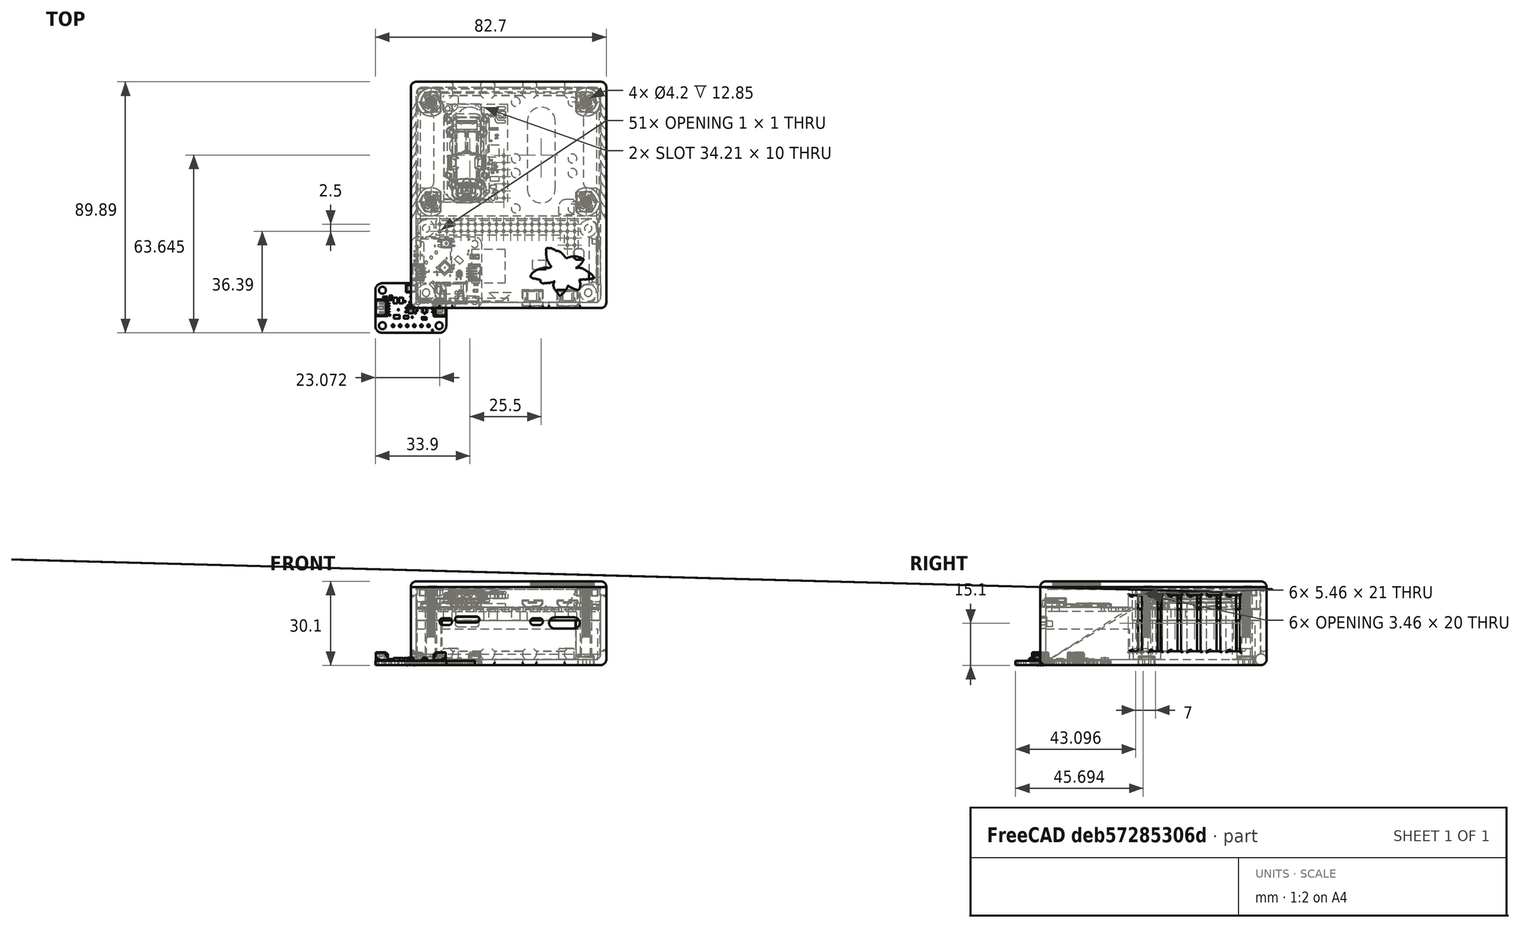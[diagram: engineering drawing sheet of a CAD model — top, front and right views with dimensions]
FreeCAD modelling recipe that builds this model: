
FCSTD DOCUMENT  (FreeCAD 0.20R29410 (Git))
Label: wearableV5
License: All rights reserved
LicenseURL: http://en.wikipedia.org/wiki/All_rights_reserved
objects: Part::Feature×60, Part::Cylinder×20, Part::MultiFuse×16, Part::Fillet×13, Sketcher::SketchObject×13, Part::Extrusion×13, App::Part×9, Part::Box×6, Part::Cut×6, Mesh::Feature×2, Part::Compound×1
note: 148 computed .brp shape members not serialized (recipe doc carries the construction recipe); baked Part::Feature solids carry a one-line shape summary decoded from their .brp

FEATURE [Part::Box] Box  label="battery"
  AttacherType = Attacher::AttachEngine3D
  Height = 11
  Length = 65
  Placement = pos=(2,2,2) rot=(0,0,1;0rad)
  Width = 30
FEATURE [Mesh::Feature] pisugar3Board
  Placement = pos=(-4.89,35.08,0.25) rot=(-1,0,0;4.71239rad)
FEATURE [Part::Feature] Part__Feature001  label="RaspberryPiZeroW"
  Placement = pos=(34.5,17,19.18) rot=(1,0,0;1.5708rad)
  shape: bbox 65.9 x 31.25 x 4.8 mm, 368 faces, 2 solids (baked)
FEATURE [Part::Feature] Part__Feature  label="ips7100"
  Placement = pos=(-24,0,222) rot=(0.999993,-0.003655,0;3.14159rad)
  shape: bbox 48.14 x 14.05 x 44.14 mm, 1935 faces (baked)
FEATURE [Part::Compound] Compound  label="ips7100s"
  Links = -> [Part__Feature]
  Placement = pos=(11.15,32.5,15.79) rot=(0,0.707107,0.707107;3.15032rad)
FEATURE [Part::Feature] Part__Feature002  label="Printed Circuit Board"
  shape: bbox 25.4 x 17.78 x 1.6 mm, 42 faces (baked)
FEATURE [Part::Feature] Part__Feature003  label="EAHC2835WD6"
  shape: bbox 3.513 x 2.813 x 0.7485 mm, 108 faces, 4 solids (baked)
FEATURE [Part::Feature] Part__Feature004  label="AS7341 v2"
  Placement = pos=(0,-0.339822,1.6) rot=(0,0,1;0rad)
  shape: bbox 2 x 3.1 x 1.1 mm, 267 faces, 26 solids (baked)
FEATURE [Part::Feature] Part__Feature005  label="CAPC-0805-T0.95-BN v1"
  Placement = pos=(-5.01759,-3.15294,1.6) rot=(0,0,1;0rad)
  shape: bbox 2.1 x 1.35 x 0.95 mm, 42 faces (baked)
FEATURE [Part::Feature] Part__Feature006  label="CAPC-0805-T0.95-BN v002"
  Placement = pos=(-5.48627,2.66154,1.6) rot=(0,0,-1;1.5708rad)
  shape: bbox 1.35 x 2.1 x 0.95 mm, 42 faces (baked)
FEATURE [Part::Feature] Part__Feature007  label="CAPC-0805-T0.95-BN v003"
  Placement = pos=(-3.43627,2.66154,1.6) rot=(0,0,-1;1.5708rad)
  shape: bbox 1.35 x 2.1 x 0.95 mm, 42 faces (baked)
FEATURE [Part::Feature] Part__Feature008  label="CAPC-0603-T0.9-BN v1"
  Placement = pos=(-1.69987,-3.28475,1.6) rot=(0,0,1;0rad)
  shape: bbox 1.7 x 0.9 x 0.9 mm, 42 faces (baked)
FEATURE [Part::Feature] Part__Feature009  label="BODY_MF06A"
  Placement = pos=(0,0,0.762) rot=(0.57735,-0.57735,-0.57735;2.0944rad)
  shape: bbox 1.601 x 2.921 x 1.016 mm, 42 faces (baked)
FEATURE [Part::Feature] Part__Feature010  label="LEAD_MF06A"
  Placement = pos=(-0.9652,-0.9525,0.1016) rot=(0.57735,-0.57735,-0.57735;2.0944rad)
  shape: bbox 0.6223 x 0.3749 x 0.8636 mm, 14 faces (baked)
FEATURE [Part::Feature] Part__Feature011  label="LEAD_MF06A001"
  Placement = pos=(-0.9652,0,0.1016) rot=(0.57735,-0.57735,-0.57735;2.0944rad)
  shape: bbox 0.6223 x 0.3749 x 0.8636 mm, 14 faces (baked)
FEATURE [Part::Feature] Part__Feature012  label="LEAD_MF06A002"
  Placement = pos=(-0.9652,0.9525,0.1016) rot=(0.57735,-0.57735,-0.57735;2.0944rad)
  shape: bbox 0.6223 x 0.3749 x 0.8636 mm, 14 faces (baked)
FEATURE [Part::Feature] Part__Feature013  label="LEAD_MF06A003"
  Placement = pos=(0.9652,-0.9525,0.1016) rot=(0.57735,0.57735,0.57735;2.0944rad)
  shape: bbox 0.6223 x 0.3749 x 0.8636 mm, 14 faces (baked)
FEATURE [Part::Feature] Part__Feature014  label="LEAD_MF06A004"
  Placement = pos=(0.9652,0,0.1016) rot=(0.57735,0.57735,0.57735;2.0944rad)
  shape: bbox 0.6223 x 0.3749 x 0.8636 mm, 14 faces (baked)
FEATURE [Part::Feature] Part__Feature015  label="LEAD_MF06A005"
  Placement = pos=(0.9652,0.9525,0.1016) rot=(0.57735,0.57735,0.57735;2.0944rad)
  shape: bbox 0.6223 x 0.3749 x 0.8636 mm, 14 faces (baked)
FEATURE [Part::Feature] Part__Feature016  label="SOT363 v2"
  Placement = pos=(4.97054,-0.645171,1.675) rot=(0,0,1;3.14159rad)
  shape: bbox 2.1 x 2 x 1.1 mm, 94 faces, 7 solids (baked)
FEATURE [Part::Feature] Part__Feature017  label="LED 0603 single color v1"
  Placement = pos=(-9.18406,3.72778,1.60762) rot=(0,0,1;1.5708rad)
  shape: bbox 1.961 x 0.7932 x 0.7145 mm, 63 faces, 5 solids (baked)
FEATURE [Part::Feature] Part__Feature018  label="RESC-0603 v1"
  Placement = pos=(4.83432,-3.67461,1.6) rot=(0,0,1;0rad)
  shape: bbox 1.7 x 0.9 x 0.55 mm, 52 faces, 3 solids (baked)
FEATURE [Part::Feature] Part__Feature019  label="RESC-0603 v002"
  Placement = pos=(-7.14949,3.61248,1.6) rot=(0,0,-1;1.5708rad)
  shape: bbox 0.9 x 1.7 x 0.55 mm, 52 faces, 3 solids (baked)
FEATURE [Part::Feature] Part__Feature020  label="YC164_RESPACK v1"
  Placement = pos=(2.99591,1.52916,1.6) rot=(0,0,1;0rad)
  shape: bbox 3.2 x 1.6 x 0.61 mm, 172 faces (baked)
FEATURE [Part::Feature] Part__Feature021  label="qwicc v2"
  Placement = pos=(-10.8364,0.0607456,1.65) rot=(0,0,-1;1.5708rad)
  shape: bbox 4.95 x 6 x 2.96 mm, 229 faces, 7 solids (baked)
FEATURE [Part::Feature] Part__Feature022  label="qwicc v003"
  Placement = pos=(10.8256,0.00556102,1.65) rot=(0,0,1;1.5708rad)
  shape: bbox 4.95 x 6 x 2.96 mm, 229 faces, 7 solids (baked)
FEATURE [Part::Feature] Part__Feature023  label="scd30"
  Placement = pos=(20,54,27) rot=(0.57735,0.57735,-0.57735;4.18879rad)
  shape: bbox 23.02 x 35.11 x 7.027 mm, 2292 faces, 25 solids (baked)
FEATURE [App::Part] sot_23_6_v2  label="sot-23-6 v2"
  Group = -> [Part__Feature009,Part__Feature010,Part__Feature011,Part__Feature012,Part__Feature013,Part__Feature014,Part__Feature015]
  Origin = -> Origin
  Placement = pos=(-4.47945,-0.603742,1.69152) rot=(0,0,1;0rad)
FEATURE [App::Part] Adafruit_AS7341_STEMMA_QT_v2  label="bme280"
  Group = -> [Part__Feature002,Part__Feature003,Part__Feature004,Part__Feature005,Part__Feature006,Part__Feature007,Part__Feature008,sot_23_6_v2,Part__Feature016,Part__Feature017,Part__Feature018,Part__Feature019,Part__Feature020,Part__Feature021,Part__Feature022]
  Origin = -> Origin001
  Placement = pos=(47.7,42,20) rot=(0,0,1;0rad)
FEATURE [Part::Box] Box002  label="bottom"
  AttacherType = Attacher::AttachEngine3D
  Height = 28
  Length = 70
  Width = 81
FEATURE [Part::Fillet] Fillet  label="bottom002"
  Base = -> Box002
  Edges = 8 edges r=2: [Edge1,Edge3,Edge4,Edge5,Edge7,Edge8,Edge9,Edge11]
FEATURE [Part::Box] Box003  label="bottom001"
  AttacherType = Attacher::AttachEngine3D
  Height = 39
  Length = 66
  Placement = pos=(2,2,2) rot=(0,0,1;0rad)
  Width = 77
FEATURE [Part::Fillet] Fillet001  label="bottomCut"
  Base = -> Box003
  Edges = 8 edges r=2: [Edge1,Edge3,Edge4,Edge5,Edge7,Edge8,Edge9,Edge11]
FEATURE [Part::Cut] Cut  label="bottom003"
  Base = -> Fillet
  Tool = -> Fillet001
FEATURE [Part::Cylinder] Cylinder
  Angle = 360
  AttacherType = Attacher::AttachEngine3D
  FirstAngle = 0
  Height = 14
  Placement = pos=(7.25,73.75,2) rot=(0,0,1;0rad)
  Radius = 5
  SecondAngle = 0
FEATURE [Part::Cylinder] Cylinder001
  Angle = 360
  AttacherType = Attacher::AttachEngine3D
  FirstAngle = 0
  Height = 14
  Placement = pos=(62.75,38,2) rot=(0,0,1;0rad)
  Radius = 5
  SecondAngle = 0
FEATURE [Part::Cylinder] Cylinder002
  Angle = 360
  AttacherType = Attacher::AttachEngine3D
  FirstAngle = 0
  Height = 14
  Placement = pos=(7.25,38,2) rot=(0,0,1;0rad)
  Radius = 5
  SecondAngle = 0
FEATURE [Part::Cylinder] Cylinder003
  Angle = 360
  AttacherType = Attacher::AttachEngine3D
  FirstAngle = 0
  Height = 14
  Placement = pos=(62.75,73.75,2) rot=(0,0,1;0rad)
  Radius = 5
  SecondAngle = 0
FEATURE [Part::MultiFuse] Fusion  label="basesBottomIn"
  Shapes = -> [Cylinder003,Cylinder,Cylinder001,Cylinder002]
FEATURE [Part::Feature] Part__Feature024  label="Board"
  shape: bbox 25.4 x 25.4 x 1.57 mm, 211 faces (baked)
FEATURE [Part::Feature] Part__Feature025  label="QFN24_4MM"
  Placement = pos=(12.1412,14.4526,1.57) rot=(0,0,1;3.92699rad)
  shape: bbox 5.657 x 5.657 x 0.9 mm, 172 faces (baked)
FEATURE [Part::Feature] Part__Feature026  label="Part 5"
  shape: bbox 0.48 x 0.6603 x 0.6 mm, 14 faces (baked)
FEATURE [Part::Feature] Part__Feature027  label="Part 6"
  shape: bbox 0.48 x 0.6603 x 0.6 mm, 14 faces (baked)
FEATURE [Part::Feature] Part__Feature028  label="Part 4"
  shape: bbox 0.48 x 0.6603 x 0.6 mm, 14 faces (baked)
FEATURE [Part::Feature] Part__Feature029  label="Part 3"
  shape: bbox 0.48 x 0.6603 x 0.6 mm, 14 faces (baked)
FEATURE [Part::Feature] Part__Feature030  label="Part 2"
  shape: bbox 0.48 x 0.6603 x 0.6 mm, 14 faces (baked)
FEATURE [Part::Feature] Part__Feature031  label="Part 1"
  shape: bbox 3 x 1.4 x 1 mm, 10 faces (baked)
FEATURE [App::Part] _6700497  label="36700497"
  Group = -> [Part__Feature026,Part__Feature027,Part__Feature028,Part__Feature029,Part__Feature030,Part__Feature031]
  Origin = -> Origin002
  Placement = pos=(0,0,0) rot=(0,0,1;3.14159rad)
FEATURE [App::Part] SOT23_5  label="SOT23-5"
  Group = -> [_6700497]
  Origin = -> Origin003
  Placement = pos=(2.54,6.985,1.57) rot=(0,0,1;3.14159rad)
FEATURE [Part::Feature] Part__Feature032  label="Pin1"
  shape: bbox 0.6224 x 1.252 x 1.252 mm, 37 faces (baked)
FEATURE [Part::Feature] Part__Feature033  label="Pin2"
  shape: bbox 0.6224 x 1.252 x 1.252 mm, 37 faces (baked)
FEATURE [Part::Feature] Part__Feature034  label="CeramicBody"
  shape: bbox 1.8 x 1.23 x 1.23 mm, 10 faces (baked)
FEATURE [App::Part] _603_NO  label="0603-NO"
  Group = -> [Part__Feature032,Part__Feature033,Part__Feature034]
  Origin = -> Origin004
  Placement = pos=(16.51,8.382,1.57) rot=(0,0,1;0rad)
FEATURE [Part::Feature] Part__Feature035  label="0603-NO (1)"
  Placement = pos=(23.241,6.223,1.57) rot=(0,0,1;0rad)
  shape: bbox 1.7 x 0.9 x 0.55 mm, 52 faces, 3 solids (baked)
FEATURE [Part::Feature] Part__Feature036  label="0603-NO (2)"
  Placement = pos=(13.3858,8.4328,1.57) rot=(0,0,1;0rad)
  shape: bbox 1.7 x 0.9 x 0.55 mm, 52 faces, 3 solids (baked)
FEATURE [Part::Feature] Part__Feature037  label="0603-NO (3)"
  Placement = pos=(1.905,18.923,1.57) rot=(0,0,1;3.14159rad)
  shape: bbox 1.7 x 0.9 x 0.55 mm, 52 faces, 3 solids (baked)
FEATURE [Part::Feature] Part__Feature038  label="Pin1 (1)"
  shape: bbox 0.6224 x 1.252 x 1.252 mm, 37 faces (baked)
FEATURE [Part::Feature] Part__Feature039  label="Pin2 (1)"
  shape: bbox 0.6224 x 1.252 x 1.252 mm, 37 faces (baked)
FEATURE [Part::Feature] Part__Feature040  label="CeramicBody (1)"
  shape: bbox 1.8 x 1.23 x 1.23 mm, 10 faces (baked)
FEATURE [App::Part] _805_NO  label="0805-NO"
  Group = -> [Part__Feature038,Part__Feature039,Part__Feature040]
  Origin = -> Origin005
  Placement = pos=(7.874,13.589,1.57) rot=(0,0,1;1.5708rad)
FEATURE [Part::Feature] Part__Feature041  label="Pin1 (2)"
  shape: bbox 0.6224 x 1.252 x 1.252 mm, 37 faces (baked)
FEATURE [Part::Feature] Part__Feature042  label="Pin2 (2)"
  shape: bbox 0.6224 x 1.252 x 1.252 mm, 37 faces (baked)
FEATURE [Part::Feature] Part__Feature043  label="CeramicBody (2)"
  shape: bbox 1.8 x 1.23 x 1.23 mm, 10 faces (baked)
FEATURE [App::Part] _805_NO__1_  label="0805-NO (1)"
  Group = -> [Part__Feature041,Part__Feature042,Part__Feature043]
  Origin = -> Origin006
  Placement = pos=(12.827,6.223,1.57) rot=(0,0,1;3.14159rad)
FEATURE [Part::Feature] Part__Feature044  label="CHIPLED_0603_NOOUTLINE"
  Placement = pos=(23.368,8.509,1.57) rot=(0,0,1;1.5708rad)
  shape: bbox 1.616 x 0.8 x 0.4 mm, 133 faces (baked)
FEATURE [Part::Feature] Part__Feature045  label="CHIPLED_0603_NOOUTLINE (1)"
  Placement = pos=(1.905,16.764,1.57) rot=(0,0,-1;1.5708rad)
  shape: bbox 1.616 x 0.8 x 0.4 mm, 133 faces (baked)
FEATURE [Part::Feature] Part__Feature046  label="JST_SH4"
  Placement = pos=(22.86,12.7,1.57) rot=(0,0,1;1.5708rad)
  shape: bbox 4.95 x 6 x 2.96 mm, 229 faces, 7 solids (baked)
FEATURE [Part::Feature] Part__Feature047  label="JST_SH4 (1)"
  Placement = pos=(2.54,12.7,1.57) rot=(0,0,-1;1.5708rad)
  shape: bbox 4.95 x 6 x 2.96 mm, 229 faces, 7 solids (baked)
FEATURE [Part::Feature] Part__Feature048  label="NEO3535_REVERSE"
  Placement = pos=(12.7,23.114,0) rot=(0,1,0;3.14159rad)
  shape: bbox 5.88 x 2.8 x 1.78 mm, 41 faces, 5 solids (baked)
FEATURE [Part::Feature] Part__Feature049  label="RESPACK_4X0603"
  Placement = pos=(22.86,18.415,1.57) rot=(0,0,1;3.14159rad)
  shape: bbox 3.2 x 1.6 x 0.61 mm, 172 faces (baked)
FEATURE [Part::Feature] Part__Feature050  label="SOT363"
  Placement = pos=(17.399,12.192,1.57) rot=(0,0,-1;1.5708rad)
  shape: bbox 2.208 x 2.208 x 1.121 mm, 178 faces, 4 solids (baked)
FEATURE [App::Part] Packages
  Group = -> [Part__Feature025,SOT23_5,_603_NO,Part__Feature035,Part__Feature036,Part__Feature037,_805_NO,_805_NO__1_,Part__Feature044,Part__Feature045,Part__Feature046,Part__Feature047,Part__Feature048,Part__Feature049,Part__Feature050]
  Origin = -> Origin007
FEATURE [App::Part] Adafruit_I2C_QT_Rotary_Encoder_v2  label="gps"
  Group = -> [Part__Feature024,Packages]
  Origin = -> Origin008
  Placement = pos=(35,51,20) rot=(0,0,1;0rad)
FEATURE [Part::Cylinder] Cylinder004
  Angle = 360
  AttacherType = Attacher::AttachEngine3D
  FirstAngle = 0
  Height = 14
  Placement = pos=(7.25,73.75,2) rot=(0,0,1;0rad)
  Radius = 2.1
  SecondAngle = 0
FEATURE [Part::Cylinder] Cylinder005
  Angle = 360
  AttacherType = Attacher::AttachEngine3D
  FirstAngle = 0
  Height = 14
  Placement = pos=(62.75,38,2) rot=(0,0,1;0rad)
  Radius = 2.1
  SecondAngle = 0
FEATURE [Part::Cylinder] Cylinder006
  Angle = 360
  AttacherType = Attacher::AttachEngine3D
  FirstAngle = 0
  Height = 14
  Placement = pos=(7.25,38,2) rot=(0,0,1;0rad)
  Radius = 2.1
  SecondAngle = 0
FEATURE [Part::Cylinder] Cylinder007
  Angle = 360
  AttacherType = Attacher::AttachEngine3D
  FirstAngle = 0
  Height = 14
  Placement = pos=(62.75,73.75,2) rot=(0,0,1;0rad)
  Radius = 2.1
  SecondAngle = 0
FEATURE [Part::MultiFuse] Fusion001  label="basesM4BottomCuts"
  Shapes = -> [Cylinder007,Cylinder004,Cylinder005,Cylinder006]
FEATURE [Sketcher::SketchObject] Sketch
  FullyConstrained = false
  expr: Constraints[40] = 67.75
  sketch-geometry (41):
    g0: LineSegment StartX=2.25 StartY=43 StartZ=0 EndX=2.25 EndY=33 EndZ=0
    g1: LineSegment StartX=2.25 StartY=33 StartZ=0 EndX=67.75 EndY=33 EndZ=0
    g2: LineSegment StartX=2.25 StartY=43 StartZ=0 EndX=8.25 EndY=43 EndZ=0
    g3: LineSegment StartX=2.25 StartY=70 StartZ=0 EndX=8.25 EndY=70 EndZ=0
    g4: LineSegment StartX=2.25 StartY=70 StartZ=0 EndX=2.25 EndY=77 EndZ=0
    g5: ArcOfCircle CenterX=4 CenterY=77 CenterZ=0 NormalX=0 NormalY=0 NormalZ=1 AngleXU=0 Radius=1.75 StartAngle=1.5708 EndAngle=3.14159
    g6: LineSegment StartX=4 StartY=78.75 StartZ=0 EndX=66 EndY=78.75 EndZ=0
    g7: ArcOfCircle CenterX=65.9989 CenterY=77 CenterZ=0 NormalX=0 NormalY=0 NormalZ=1 AngleXU=0 Radius=1.75 StartAngle=6.28258 EndAngle=7.85338
    g8: LineSegment StartX=67.7489 StartY=76.9989 StartZ=0 EndX=67.7489 EndY=70 EndZ=0
    g9: LineSegment StartX=67.7489 StartY=70 StartZ=0 EndX=61.75 EndY=70 EndZ=0
    g10: LineSegment StartX=61.75 StartY=70 StartZ=0 EndX=61.75 EndY=43 EndZ=0
    g11: LineSegment StartX=61.75 StartY=43 StartZ=0 EndX=67.75 EndY=43 EndZ=0
    g12: LineSegment StartX=67.75 StartY=43 StartZ=0 EndX=67.75 EndY=33 EndZ=0
    g13: GeomPoint X=67.75 Y=33 Z=0
    g14: GeomPoint X=67.75 Y=33 Z=0
    g15: GeomPoint X=67.75 Y=33 Z=0
    g16: GeomPoint X=67.75 Y=33 Z=0
    g17: GeomPoint X=67.75 Y=33 Z=0
    g18: LineSegment StartX=8.25 StartY=43 StartZ=0 EndX=8.25 EndY=70 EndZ=0
    g19: Circle CenterX=7.25 CenterY=73.75 CenterZ=0 NormalX=0 NormalY=0 NormalZ=1 AngleXU=0 Radius=2.1
    g20: Circle CenterX=7.25 CenterY=38 CenterZ=0 NormalX=0 NormalY=0 NormalZ=1 AngleXU=0 Radius=2.1
    g21: Circle CenterX=62.75 CenterY=38 CenterZ=0 NormalX=0 NormalY=0 NormalZ=1 AngleXU=0 Radius=2.1
    g22: Circle CenterX=62.75 CenterY=73.75 CenterZ=0 NormalX=0 NormalY=0 NormalZ=1 AngleXU=0 Radius=2.1
    g23: Circle CenterX=13.2 CenterY=71.45 CenterZ=0 NormalX=0 NormalY=0 NormalZ=1 AngleXU=0 Radius=1.6
    g24: Circle CenterX=37.54 CenterY=73.86 CenterZ=0 NormalX=0 NormalY=0 NormalZ=1 AngleXU=0 Radius=1.6
    g25: Circle CenterX=57.86 CenterY=73.86 CenterZ=0 NormalX=0 NormalY=0 NormalZ=1 AngleXU=0 Radius=1.6
    g26: Circle CenterX=37.54 CenterY=53.54 CenterZ=0 NormalX=0 NormalY=0 NormalZ=1 AngleXU=0 Radius=1.6
    g27: Circle CenterX=57.86 CenterY=53.54 CenterZ=0 NormalX=0 NormalY=0 NormalZ=1 AngleXU=0 Radius=1.6
    g28: Circle CenterX=37.54 CenterY=48.35 CenterZ=0 NormalX=0 NormalY=0 NormalZ=1 AngleXU=0 Radius=1.6
    g29: Circle CenterX=57.86 CenterY=48.35 CenterZ=0 NormalX=0 NormalY=0 NormalZ=1 AngleXU=0 Radius=1.6
    g30: Circle CenterX=37.54 CenterY=35.65 CenterZ=0 NormalX=0 NormalY=0 NormalZ=1 AngleXU=0 Radius=1.6
    g31: Circle CenterX=57.86 CenterY=35.65 CenterZ=0 NormalX=0 NormalY=0 NormalZ=1 AngleXU=0 Radius=1.6
    g32: Circle CenterX=29.425 CenterY=39.45 CenterZ=0 NormalX=0 NormalY=0 NormalZ=1 AngleXU=0 Radius=1.6
    g33: ArcOfCircle CenterX=46.7 CenterY=66.86 CenterZ=0 NormalX=0 NormalY=0 NormalZ=1 AngleXU=0 Radius=5 StartAngle=2e-16 EndAngle=3.14159
    g34: ArcOfCircle CenterX=46.7 CenterY=42.65 CenterZ=0 NormalX=0 NormalY=0 NormalZ=1 AngleXU=0 Radius=5 StartAngle=3.14159 EndAngle=6.28319
    g35: LineSegment StartX=41.7 StartY=66.86 StartZ=0 EndX=41.7 EndY=42.65 EndZ=0
    g36: LineSegment StartX=51.7 StartY=42.65 StartZ=0 EndX=51.7 EndY=66.86 EndZ=0
    g37: ArcOfCircle CenterX=21.2 CenterY=66.86 CenterZ=0 NormalX=0 NormalY=0 NormalZ=1 AngleXU=0 Radius=5 StartAngle=0 EndAngle=3.14159
    g38: ArcOfCircle CenterX=21.2 CenterY=42.65 CenterZ=0 NormalX=0 NormalY=0 NormalZ=1 AngleXU=0 Radius=5 StartAngle=3.14159 EndAngle=6.28319
    g39: LineSegment StartX=16.2 StartY=66.86 StartZ=0 EndX=16.2 EndY=42.65 EndZ=0
    g40: LineSegment StartX=26.2 StartY=42.65 StartZ=0 EndX=26.2 EndY=66.86 EndZ=0
  constraints (110):
    c: Vertical(g0)
    c: Coincident(g1,g0)
    c: Horizontal(g1)
    c: Coincident(g2,g0)
    c: Coincident(g4,g3)
    c: Vertical(g4)
    c: Coincident(g5,g4)
    c: Horizontal(g6)
    c: Coincident(g7,g6)
    c: Coincident(g8,g7)
    c: Coincident(g9,g8)
    c: Horizontal(g9)
    c: Coincident(g10,g9)
    c: Vertical(g10)
    c: Horizontal(g11)
    c: DistanceX(g-1,g0) = 2.25
    c: Horizontal(g2)
    c: Coincident(g13,g12)
    c: Coincident(g14,g1)
    c: Coincident(g15,g12)
    c: Coincident(g16,g1)
    c: Coincident(g17,g12)
    c: Coincident(g12,g1)
    c: Vertical(g12)
    c: Coincident(g5,g6)
    c: Coincident(g18,g2)
    c: Coincident(g18,g3)
    c: Vertical(g18)
    c: Horizontal(g3)
    c: Vertical(g8)
    c: DistanceY(g0) = 33
    c: DistanceX(g0,g2) = 6
    c: DistanceY(g0,g0) = 10
    c: DistanceX(g3,g3) = 6
    c: DistanceY(g18,g18) = 27
    c: DistanceY(g4,g4) = 7
    c: DistanceY(g5) = 77
    c: Angle(g5) = 1.5708
    c: Radius(g7) = 1.75
    c: Angle(g7) = 1.5708
    c: DistanceX(g1) = 67.75
    c: Coincident(g11,g12)
    c: DistanceY(g1,g11) = 10
    c: Coincident(g10,g11)
    c: DistanceX(g11,g11) = 6
    c: DistanceX(g6,g6) = 62
    c: Radius(g19) = 2.1
    c: DistanceX(g20) = 7.25
    c: DistanceY(g20) = 38
    c: Radius(g20) = 2.1
    c: DistanceX(g21) = 62.75
    c: DistanceY(g20,g21) = 0
    c: Radius(g21) = 2.1
    c: DistanceX(g22,g21) = 0
    c: Radius(g22) = 2.1
    c: DistanceX(g19,g22) = 55.5
    c: DistanceY(g19) = 73.75
    c: DistanceY(g19,g22) = 0
    c: DistanceY(g3,g8) = 0
    c: DistanceX(g5) = 4
    c: DistanceX(g24) = 37.54
    c: Radius(g24) = 1.6
    c: DistanceY(g24,g25) = 0
    c: Radius(g25) = 1.6
    c: DistanceX(g24,g25) = 20.32
    c: DistanceY(g24) = 73.86
    c: DistanceX(g26,g24) = 0
    c: Radius(g26) = 1.6
    c: DistanceY(g26,g24) = 20.32
    c: DistanceY(g27,g26) = 0
    c: DistanceX(g27,g25) = 0
    c: Radius(g27) = 1.6
    c: DistanceX(g28,g26) = 0
    c: DistanceY(g28) = 48.35
    c: Radius(g28) = 1.6
    c: DistanceY(g28,g29) = 0
    c: DistanceX(g27,g29) = 0
    c: Radius(g29) = 1.6
    c: DistanceX(g28,g30) = 0
    c: DistanceX(g31,g29) = 0
    c: DistanceY(g30,g28) = 12.7
    c: DistanceY(g31,g30) = 0
    c: Radius(g31) = 1.6
    c: Radius(g30) = 1.6
    c: Radius(g32) = 1.6
    c: DistanceY(g32) = 39.45
    c: DistanceX(g32) = 29.425
    c: DistanceY(g32,g23) = 32
    c: DistanceX(g23,g32) = 16.225
    c: Radius(g23) = 1.6
    c: Tangent(g33,g35) = -1.5708
    c: Tangent(g35,g34) = -1.5708
    c: Tangent(g34,g36) = -1.5708
    c: Tangent(g36,g33) = -1.5708
    c: Equal(g33,g34)
    c: Vertical(g35)
    c: DistanceX(g33) = 46.7
    c: DistanceY(g33,g24) = 7
    c: DistanceY(g30,g34) = 7
    c: Radius(g33) = 5
    c: Tangent(g37,g39) = -1.5708
    c: Tangent(g39,g38) = -1.5708
    c: Tangent(g38,g40) = -1.5708
    c: Tangent(g40,g37) = -1.5708
    c: Equal(g37,g38)
    c: Vertical(g39)
    c: Radius(g37) = 5
    c: DistanceY(g37,g33) = 0
    c: DistanceY(g34,g38) = 0
    c: DistanceX(g23,g37) = 8
FEATURE [Part::Extrusion] Extrude  label="sensorHold"
  Base = -> Sketch
  Dir = (0,0,1)
  DirMode = 2
  FaceMakerClass = Part::FaceMakerBullseye
  LengthFwd = 4
  LengthRev = 0
  Placement = pos=(0,0,16) rot=(0,0,1;0rad)
  Solid = true
  Symmetric = false
FEATURE [Part::Fillet] Fillet002  label="sensorHold001"
  Base = -> Extrude
  Edges = 10 edges r=2: [Edge1,Edge2,Edge5,Edge8,Edge11,Edge14,Edge17,Edge20,Edge35,Edge38]
FEATURE [Sketcher::SketchObject] Sketch001
  FullyConstrained = true
  sketch-geometry (10):
    g0: LineSegment StartX=17.025 StartY=72.94 StartZ=0 EndX=17.025 EndY=75.94 EndZ=0
    g1: LineSegment StartX=14.525 StartY=70.44 StartZ=0 EndX=11.525 EndY=70.44 EndZ=0
    g2: LineSegment StartX=11.525 StartY=70.44 StartZ=0 EndX=11.525 EndY=75.94 EndZ=0
    g3: LineSegment StartX=17.025 StartY=75.94 StartZ=0 EndX=11.525 EndY=75.94 EndZ=0
    g4: ArcOfCircle CenterX=14.525 CenterY=72.94 CenterZ=0 NormalX=0 NormalY=0 NormalZ=1 AngleXU=0 Radius=2.5 StartAngle=4.71239 EndAngle=6.28319
    g5: LineSegment StartX=58.525 StartY=33.36 StartZ=0 EndX=53.025 EndY=33.36 EndZ=0
    g6: LineSegment StartX=53.025 StartY=33.36 StartZ=0 EndX=53.025 EndY=36.36 EndZ=0
    g7: LineSegment StartX=58.525 StartY=33.36 StartZ=0 EndX=58.525 EndY=38.86 EndZ=0
    g8: LineSegment StartX=58.525 StartY=38.86 StartZ=0 EndX=55.525 EndY=38.86 EndZ=0
    g9: ArcOfCircle CenterX=55.525 CenterY=36.36 CenterZ=0 NormalX=0 NormalY=0 NormalZ=1 AngleXU=0 Radius=2.5 StartAngle=1.5708 EndAngle=3.14159
  constraints (32):
    c: Vertical(g0)
    c: Horizontal(g1)
    c: Vertical(g2)
    c: Coincident(g2,g3)
    c: Coincident(g0,g3)
    c: Horizontal(g3)
    c: DistanceX(g3,g3) = 5.5
    c: DistanceY(g2,g2) = 5.5
    c: DistanceY(g4,g4) = 0
    c: DistanceX(g4,g4) = 0
    c: Coincident(g1,g4)
    c: Coincident(g0,g4)
    c: Radius(g4) = 2.5
    c: DistanceX(g4) = 14.525
    c: DistanceY(g4) = 72.94
    c: Coincident(g1,g2)
    c: Horizontal(g5)
    c: Vertical(g6)
    c: Vertical(g7)
    c: Horizontal(g8)
    c: Coincident(g7,g8)
    c: Coincident(g8,g9)
    c: Coincident(g6,g9)
    c: Coincident(g5,g6)
    c: Coincident(g5,g7)
    c: DistanceX(g5,g5) = 5.5
    c: DistanceY(g7,g7) = 5.5
    c: DistanceY(g6,g6) = 3
    c: DistanceX(g8,g8) = 3
    c: Radius(g9) = 2.5
    c: DistanceY(g9,g4) = 36.58
    c: DistanceX(g4,g9) = 41
FEATURE [Part::Extrusion] Extrude001
  Base = -> Sketch001
  Dir = (0,0,1)
  DirMode = 2
  FaceMakerClass = Part::FaceMakerBullseye
  LengthFwd = 4
  LengthRev = 0
  Placement = pos=(0,0,2) rot=(0,0,1;0rad)
  Solid = true
  Symmetric = false
FEATURE [Part::Fillet] Fillet003  label="ipsHoldBottomIn"
  Base = -> Extrude001
  Edges = 14 edges r=0.5: [Edge4,Edge7,Edge10,Edge11,Edge13,Edge15,Edge19,Edge20,Edge22,Edge23,Edge25,Edge26,Edge28,Edge30]
FEATURE [Sketcher::SketchObject] Sketch002
  FullyConstrained = true
  MapMode = 2
  Support = -> [Cut]
  sketch-geometry (10):
    g0: LineSegment StartX=60.5 StartY=8.4 StartZ=0 EndX=68.5 EndY=8.4 EndZ=0
    g1: LineSegment StartX=68.5 StartY=8.4 StartZ=0 EndX=68.5 EndY=1.5 EndZ=0
    g2: LineSegment StartX=68.5 StartY=1.5 StartZ=0 EndX=60.5 EndY=1.5 EndZ=0
    g3: LineSegment StartX=60.5 StartY=1.5 StartZ=0 EndX=60.5 EndY=8.4 EndZ=0
    g4: LineSegment StartX=1.5 StartY=9 StartZ=0 EndX=8.75 EndY=9 EndZ=0
    g5: LineSegment StartX=8.75 StartY=9 StartZ=0 EndX=8.75 EndY=1.5 EndZ=0
    g6: LineSegment StartX=8.75 StartY=1.5 StartZ=0 EndX=1.5 EndY=1.5 EndZ=0
    g7: LineSegment StartX=1.5 StartY=1.5 StartZ=0 EndX=1.5 EndY=9 EndZ=0
    g8: Circle CenterX=5.475 CenterY=5.475 CenterZ=0 NormalX=0 NormalY=0 NormalZ=1 AngleXU=0 Radius=1.35
    g9: Circle CenterX=63.525 CenterY=5.475 CenterZ=0 NormalX=0 NormalY=0 NormalZ=1 AngleXU=0 Radius=1.35
  constraints (30):
    c: Coincident(g0,g1)
    c: Coincident(g1,g2)
    c: Coincident(g2,g3)
    c: Coincident(g3,g0)
    c: Horizontal(g0)
    c: Horizontal(g2)
    c: Vertical(g1)
    c: Vertical(g3)
    c: Coincident(g4,g5)
    c: Coincident(g5,g6)
    c: Coincident(g6,g7)
    c: Coincident(g7,g4)
    c: Horizontal(g4)
    c: Horizontal(g6)
    c: Vertical(g5)
    c: Vertical(g7)
    c: DistanceX(g6) = 1.5
    c: DistanceY(g6) = 1.5
    c: DistanceX(g6,g6) = 7.25
    c: DistanceY(g7,g7) = 7.5
    c: DistanceX(g-1,g1) = 68.5
    c: DistanceY(g2,g5) = 0
    c: DistanceY(g0,g4) = 0.6
    c: DistanceX(g2,g2) = 8
    c: DistanceX(g8) = 5.475
    c: Radius(g8) = 1.35
    c: DistanceX(g9) = 63.525
    c: DistanceY(g8,g9) = 0
    c: Radius(g9) = 1.35
    c: DistanceY(g8) = 5.475
FEATURE [Part::Extrusion] Extrude002  label="RaberryPiHold"
  Base = -> Sketch002
  Dir = (0,0,1)
  DirMode = 2
  FaceMakerClass = Part::FaceMakerBullseye
  LengthFwd = 2
  LengthRev = 0
  Placement = pos=(0,0,20.7) rot=(0,0,1;0rad)
  Solid = true
  Symmetric = false
FEATURE [Part::Fillet] Fillet004  label="piHoldBottomIn"
  Base = -> Extrude002
  Edges = 6 edges: [Edge1 r=2,Edge4 r=1,Edge12 r=1,Edge17 r=2,Edge19 r=1,Edge22 r=1]
FEATURE [Part::Box] Box004  label="top"
  AttacherType = Attacher::AttachEngine3D
  Height = 2
  Length = 70
  Placement = pos=(0,0,28) rot=(0,0,1;0rad)
  Width = 81
FEATURE [Part::Fillet] Fillet005  label="top001"
  Base = -> Box004
  Edges = 8 edges r=1.95: [Edge1,Edge2,Edge3,Edge5,Edge6,Edge7,Edge10,Edge12]
FEATURE [Part::Feature] Part__Feature052  label="m4s"
  Placement = pos=(62.75,73.75,14) rot=(1,0,0;3.14159rad)
  shape: bbox 5.501 x 5.501 x 28.29 mm, 108 faces (baked)
FEATURE [Part::Feature] Part__Feature053  label="m4s001"
  Placement = pos=(7.25,73.75,14) rot=(1,0,0;3.14159rad)
  shape: bbox 5.501 x 5.501 x 28.29 mm, 108 faces (baked)
FEATURE [Part::Feature] Part__Feature054  label="m4s002"
  Placement = pos=(62.75,38,14) rot=(1,0,0;3.14159rad)
  shape: bbox 5.501 x 5.501 x 28.29 mm, 108 faces (baked)
FEATURE [Part::Feature] Part__Feature055  label="m4s003"
  Placement = pos=(7.25,38,14) rot=(1,0,0;3.14159rad)
  shape: bbox 5.501 x 5.501 x 28.29 mm, 108 faces (baked)
FEATURE [Part::Cylinder] Cylinder008
  Angle = 360
  AttacherType = Attacher::AttachEngine3D
  FirstAngle = 0
  Height = 7.75
  Placement = pos=(7.25,73.75,2) rot=(0,0,1;0rad)
  Radius = 5
  SecondAngle = 0
FEATURE [Part::Cylinder] Cylinder009
  Angle = 360
  AttacherType = Attacher::AttachEngine3D
  FirstAngle = 0
  Height = 7.75
  Placement = pos=(62.75,38,2) rot=(0,0,1;0rad)
  Radius = 5
  SecondAngle = 0
FEATURE [Part::Cylinder] Cylinder010
  Angle = 360
  AttacherType = Attacher::AttachEngine3D
  FirstAngle = 0
  Height = 7.75
  Placement = pos=(7.25,38,2) rot=(0,0,1;0rad)
  Radius = 5
  SecondAngle = 0
FEATURE [Part::Cylinder] Cylinder011
  Angle = 360
  AttacherType = Attacher::AttachEngine3D
  FirstAngle = 0
  Height = 7.75
  Placement = pos=(62.75,73.75,2) rot=(0,0,1;0rad)
  Radius = 5
  SecondAngle = 0
FEATURE [Part::MultiFuse] Fusion002  label="m4BaseTopIn"
  Placement = pos=(70,0,30) rot=(0,1,0;3.14159rad)
  Shapes = -> [Cylinder011,Cylinder008,Cylinder009,Cylinder010]
FEATURE [Part::Feature] Part__Feature056  label="m4Nut"
  Placement = pos=(7.25,38,27) rot=(0,0,1;1.5708rad)
  shape: bbox 8.084 x 8.084 x 2.714 mm, 34 faces (baked)
FEATURE [Part::MultiFuse] Fusion003  label="m4s004"
  Shapes = -> [Part__Feature055,Part__Feature052,Part__Feature053,Part__Feature054]
FEATURE [Part::Feature] Part__Feature057  label="m4Nut001"
  Placement = pos=(62.75,38,27) rot=(0,0,1;1.5708rad)
  shape: bbox 8.084 x 8.084 x 2.714 mm, 34 faces (baked)
FEATURE [Part::MultiFuse] Fusion004
  Shapes = -> [Part__Feature056,Part__Feature057]
FEATURE [Part::Feature] Part__Feature058  label="m4Nut002"
  Placement = pos=(7.25,38,27) rot=(0,0,1;1.5708rad)
  shape: bbox 8.084 x 8.084 x 2.714 mm, 34 faces (baked)
FEATURE [Part::Feature] Part__Feature059  label="m4Nut003"
  Placement = pos=(62.75,38,27) rot=(0,0,1;1.5708rad)
  shape: bbox 8.084 x 8.084 x 2.714 mm, 34 faces (baked)
FEATURE [Part::MultiFuse] Fusion005
  Placement = pos=(0,35.75,0) rot=(0,0,1;0rad)
  Shapes = -> [Part__Feature058,Part__Feature059]
FEATURE [Part::MultiFuse] Fusion006  label="m4Nuts"
  Placement = pos=(0,0,-1) rot=(0,0,1;0rad)
  Shapes = -> [Fusion005,Fusion004]
FEATURE [Sketcher::SketchObject] Sketch003
  FullyConstrained = true
  MapMode = 2
  Placement = pos=(70,0,30) rot=(0,1,0;3.14159rad)
  Support = -> [Fusion002]
  sketch-geometry (36):
    g0: LineSegment StartX=5.125 StartY=34.3194 StartZ=0 EndX=9.375 EndY=34.3194 EndZ=0
    g1: LineSegment StartX=9.375 StartY=34.3194 StartZ=0 EndX=9.47604 EndY=34.4944 EndZ=0
    g2: LineSegment StartX=5.125 StartY=34.3194 StartZ=0 EndX=3 EndY=38 EndZ=0
    g3: LineSegment StartX=3 StartY=38 StartZ=0 EndX=5.125 EndY=41.6806 EndZ=0
    g4: LineSegment StartX=5.125 StartY=41.6806 StartZ=0 EndX=9.375 EndY=41.6806 EndZ=0
    g5: LineSegment StartX=9.375 StartY=41.6806 StartZ=0 EndX=9.47604 EndY=41.5056 EndZ=0
    g6: LineSegment StartX=9.47604 StartY=41.5056 StartZ=0 EndX=12.476 EndY=41.5056 EndZ=0
    g7: LineSegment StartX=12.476 StartY=41.5056 StartZ=0 EndX=12.476 EndY=34.4944 EndZ=0
    g8: LineSegment StartX=12.476 StartY=34.4944 StartZ=0 EndX=9.47604 EndY=34.4944 EndZ=0
    g9: LineSegment StartX=60.524 StartY=34.4944 StartZ=0 EndX=60.625 EndY=34.3194 EndZ=0
    g10: LineSegment StartX=60.625 StartY=34.3194 StartZ=0 EndX=64.875 EndY=34.3194 EndZ=0
    g11: LineSegment StartX=64.875 StartY=34.3194 StartZ=0 EndX=67 EndY=38 EndZ=0
    g12: LineSegment StartX=67 StartY=38 StartZ=0 EndX=64.875 EndY=41.6806 EndZ=0
    g13: LineSegment StartX=64.875 StartY=41.6806 StartZ=0 EndX=60.625 EndY=41.6806 EndZ=0
    g14: LineSegment StartX=60.625 StartY=41.6806 StartZ=0 EndX=60.524 EndY=41.5056 EndZ=0
    g15: LineSegment StartX=60.524 StartY=41.5056 StartZ=0 EndX=57.524 EndY=41.5056 EndZ=0
    g16: LineSegment StartX=57.524 StartY=41.5056 StartZ=0 EndX=57.524 EndY=34.4944 EndZ=0
    g17: LineSegment StartX=57.524 StartY=34.4944 StartZ=0 EndX=60.524 EndY=34.4944 EndZ=0
    g18: LineSegment StartX=3 StartY=73.75 StartZ=0 EndX=5.125 EndY=70.0694 EndZ=0
    g19: LineSegment StartX=5.125 StartY=70.0694 StartZ=0 EndX=9.375 EndY=70.0694 EndZ=0
    g20: LineSegment StartX=9.375 StartY=70.0694 StartZ=0 EndX=9.47604 EndY=70.2444 EndZ=0
    g21: LineSegment StartX=9.47604 StartY=70.2444 StartZ=0 EndX=12.476 EndY=70.2444 EndZ=0
    g22: LineSegment StartX=12.476 StartY=70.2444 StartZ=0 EndX=12.476 EndY=77.2556 EndZ=0
    g23: LineSegment StartX=12.476 StartY=77.2556 StartZ=0 EndX=9.47604 EndY=77.2556 EndZ=0
    g24: LineSegment StartX=9.47604 StartY=77.2556 StartZ=0 EndX=9.375 EndY=77.4306 EndZ=0
    g25: LineSegment StartX=9.375 StartY=77.4306 StartZ=0 EndX=5.125 EndY=77.4306 EndZ=0
    g26: LineSegment StartX=5.125 StartY=77.4306 StartZ=0 EndX=3 EndY=73.75 EndZ=0
    g27: LineSegment StartX=67 StartY=73.75 StartZ=0 EndX=64.875 EndY=70.0694 EndZ=0
    g28: LineSegment StartX=64.875 StartY=70.0694 StartZ=0 EndX=60.625 EndY=70.0694 EndZ=0
    g29: LineSegment StartX=60.625 StartY=70.0694 StartZ=0 EndX=60.524 EndY=70.2444 EndZ=0
    g30: LineSegment StartX=60.524 StartY=70.2444 StartZ=0 EndX=57.524 EndY=70.2444 EndZ=0
    g31: LineSegment StartX=57.524 StartY=70.2444 StartZ=0 EndX=57.524 EndY=77.2556 EndZ=0
    g32: LineSegment StartX=57.524 StartY=77.2556 StartZ=0 EndX=60.524 EndY=77.2556 EndZ=0
    g33: LineSegment StartX=60.524 StartY=77.2556 StartZ=0 EndX=60.625 EndY=77.4306 EndZ=0
    g34: LineSegment StartX=60.625 StartY=77.4306 StartZ=0 EndX=64.875 EndY=77.4306 EndZ=0
    g35: LineSegment StartX=64.875 StartY=77.4306 StartZ=0 EndX=67 EndY=73.75 EndZ=0
  constraints (108):
    c: Horizontal(g0)
    c: Coincident(g1,g0)
    c: Coincident(g2,g0)
    c: Coincident(g4,g3)
    c: Horizontal(g4)
    c: Coincident(g5,g4)
    c: Coincident(g6,g5)
    c: Horizontal(g6)
    c: Coincident(g7,g6)
    c: Vertical(g7)
    c: Coincident(g8,g7)
    c: Coincident(g8,g1)
    c: Angle(g0,g2) = 2.0944
    c: Coincident(g2,g3)
    c: Distance(g2) = 4.25
    c: Distance(g3) = 4.25
    c: DistanceY(g2) = 38
    c: Angle(g3,g4) = 2.0944
    c: DistanceX(g2) = 3
    c: Distance(g4) = 4.25
    c: Distance(g0) = 4.25
    c: Angle(g4,g5) = 2.0944
    c: Angle(g1,g0) = 2.0944
    c: DistanceY(g1,g1) = 0.175
    c: Horizontal(g8)
    c: DistanceX(g8,g8) = 3
    c: Coincident(g10,g9)
    c: Horizontal(g10)
    c: Coincident(g11,g10)
    c: Coincident(g15,g14)
    c: Horizontal(g15)
    c: Coincident(g16,g15)
    c: Vertical(g16)
    c: Coincident(g17,g16)
    c: Coincident(g17,g9)
    c: Horizontal(g17)
    c: Angle(g11,g10) = 2.0944
    c: Angle(g12,g11) = 2.0944
    c: Coincident(g11,g12)
    c: Angle(g13,g12) = 2.0944
    c: Coincident(g13,g14)
    c: Coincident(g12,g13)
    c: Angle(g14,g13) = 2.0944
    c: Angle(g10,g9) = 2.0944
    c: DistanceX(g14,g9) = 0
    c: DistanceX(g13,g9) = 0
    c: Distance(g10) = 4.25
    c: Distance(g11) = 4.25
    c: Distance(g13) = 4.25
    c: DistanceX(g17,g17) = 3
    c: DistanceY(g5,g4) = 0.175
    c: DistanceX(g2,g11) = 64
    c: DistanceY(g11,g2) = 0
    c: DistanceY(g15,g6) = 0
    c: Coincident(g18,g19)
    c: Horizontal(g19)
    c: Coincident(g19,g20)
    c: Coincident(g20,g21)
    c: Horizontal(g21)
    c: Coincident(g21,g22)
    c: Vertical(g22)
    c: Coincident(g22,g23)
    c: Coincident(g23,g24)
    c: Coincident(g24,g25)
    c: Horizontal(g25)
    c: Coincident(g25,g26)
    c: Coincident(g26,g18)
    c: DistanceX(g18,g2) = 0
    c: DistanceY(g2,g18) = 35.75
    c: Angle(g18,g26) = 2.0944
    c: Angle(g26,g25) = 2.0944
    c: Angle(g20,g19) = 2.0944
    c: Angle(g25,g24) = 2.0944
    c: DistanceY(g23,g24) = 0.175
    c: DistanceY(g19,g20) = 0.175
    c: Distance(g21) = 3
    c: Horizontal(g23)
    c: Coincident(g27,g28)
    c: Horizontal(g28)
    c: Coincident(g28,g29)
    c: Coincident(g29,g30)
    c: Horizontal(g30)
    c: Coincident(g30,g31)
    c: Vertical(g31)
    c: Coincident(g31,g32)
    c: Horizontal(g32)
    c: Coincident(g32,g33)
    c: Coincident(g33,g34)
    c: Horizontal(g34)
    c: Coincident(g34,g35)
    c: Coincident(g35,g27)
    c: DistanceX(g11,g27) = 0
    c: DistanceY(g18,g27) = 0
    c: Angle(g27,g28) = 2.0944
    c: Angle(g35,g27) = 2.0944
    c: Angle(g33,g34) = 2.0944
    c: DistanceX(g32,g32) = 3
    c: Angle(g28,g29) = 2.0944
    c: DistanceY(g28,g29) = 0.175
    c: DistanceY(g32,g33) = 0.175
    c: DistanceX(g30,g15) = 0
    c: Distance(g18) = 4.25
    c: Distance(g26) = 4.25
    c: Distance(g19) = 4.25
    c: Distance(g25) = 4.25
    c: Distance(g28) = 4.25
    c: Distance(g27) = 4.25
    c: Distance(g35) = 4.25
FEATURE [Part::Extrusion] Extrude003  label="m4InletTopCut"
  Base = -> Sketch003
  Dir = (0,0,-1)
  DirMode = 2
  FaceMakerClass = Part::FaceMakerBullseye
  LengthFwd = 2.5
  LengthRev = 0
  Placement = pos=(0,0,-2.75) rot=(0,0,1;0rad)
  Solid = true
  Symmetric = false
FEATURE [Part::Box] Box005  label="baseTopCut"
  AttacherType = Attacher::AttachEngine3D
  Height = 8
  Length = 49
  Placement = pos=(10.5,33.5,20) rot=(0,0,1;0rad)
  Width = 44
FEATURE [Part::Feature] Part__Feature060  label="logoTopCut"
  Placement = pos=(23,-2,35) rot=(-1,0,0;1.5708rad)
  shape: bbox 22.79 x 17.08 x 8 mm, 886 faces (baked)
FEATURE [Mesh::Feature] mintsLogo80P___90CutBase  label="mintsLogo80P - 90CutBase"
  Placement = pos=(54.35,12.9,26) rot=(0,0,1;0rad)
FEATURE [Part::Cylinder] Cylinder012
  Angle = 360
  AttacherType = Attacher::AttachEngine3D
  FirstAngle = 0
  Height = 3.15
  Placement = pos=(7.25,73.75,2) rot=(0,0,1;0rad)
  Radius = 3
  SecondAngle = 0
FEATURE [Part::Cylinder] Cylinder013
  Angle = 360
  AttacherType = Attacher::AttachEngine3D
  FirstAngle = 0
  Height = 3.15
  Placement = pos=(62.75,38,2) rot=(0,0,1;0rad)
  Radius = 3
  SecondAngle = 0
FEATURE [Part::Cylinder] Cylinder014
  Angle = 360
  AttacherType = Attacher::AttachEngine3D
  FirstAngle = 0
  Height = 3.15
  Placement = pos=(7.25,38,2) rot=(0,0,1;0rad)
  Radius = 3
  SecondAngle = 0
FEATURE [Part::Cylinder] Cylinder015
  Angle = 360
  AttacherType = Attacher::AttachEngine3D
  FirstAngle = 0
  Height = 3.15
  Placement = pos=(62.75,73.75,2) rot=(0,0,1;0rad)
  Radius = 3
  SecondAngle = 0
FEATURE [Part::MultiFuse] Fusion007  label="m4headBottomCut"
  Placement = pos=(0,0,-2) rot=(0,0,1;0rad)
  Shapes = -> [Cylinder015,Cylinder012,Cylinder013,Cylinder014]
FEATURE [Sketcher::SketchObject] Sketch004
  FullyConstrained = true
  Placement = pos=(0,0,0) rot=(1,0,0;1.5708rad)
  sketch-geometry (16):
    g0: ArcOfCircle CenterX=11.55 CenterY=15.58 CenterZ=0 NormalX=0 NormalY=0 NormalZ=1 AngleXU=0 Radius=1.25 StartAngle=1.5708 EndAngle=4.71239
    g1: ArcOfCircle CenterX=13.55 CenterY=15.58 CenterZ=0 NormalX=0 NormalY=0 NormalZ=1 AngleXU=0 Radius=1.25 StartAngle=4.71239 EndAngle=7.85398
    g2: LineSegment StartX=11.55 StartY=14.33 StartZ=0 EndX=13.55 EndY=14.33 EndZ=0
    g3: LineSegment StartX=13.55 StartY=16.83 StartZ=0 EndX=11.55 EndY=16.83 EndZ=0
    g4: ArcOfCircle CenterX=44.02 CenterY=15.58 CenterZ=0 NormalX=0 NormalY=0 NormalZ=1 AngleXU=0 Radius=1.25 StartAngle=1.5708 EndAngle=4.71239
    g5: ArcOfCircle CenterX=46.02 CenterY=15.58 CenterZ=0 NormalX=0 NormalY=0 NormalZ=1 AngleXU=0 Radius=1.25 StartAngle=4.71239 EndAngle=7.85398
    g6: LineSegment StartX=44.02 StartY=14.33 StartZ=0 EndX=46.02 EndY=14.33 EndZ=0
    g7: LineSegment StartX=46.02 StartY=16.83 StartZ=0 EndX=44.02 EndY=16.83 EndZ=0
    g8: ArcOfCircle CenterX=16.9 CenterY=16.35 CenterZ=0 NormalX=0 NormalY=0 NormalZ=1 AngleXU=0 Radius=1.075 StartAngle=1.5708 EndAngle=4.71239
    g9: ArcOfCircle CenterX=23.5 CenterY=16.35 CenterZ=0 NormalX=0 NormalY=0 NormalZ=1 AngleXU=0 Radius=1.075 StartAngle=4.71239 EndAngle=7.85398
    g10: LineSegment StartX=16.9 StartY=15.275 StartZ=0 EndX=23.5 EndY=15.275 EndZ=0
    g11: LineSegment StartX=23.5 StartY=17.425 StartZ=0 EndX=16.9 EndY=17.425 EndZ=0
    g12: ArcOfCircle CenterX=51.5 CenterY=15.1 CenterZ=0 NormalX=0 NormalY=0 NormalZ=1 AngleXU=0 Radius=2 StartAngle=1.5708 EndAngle=4.71239
    g13: ArcOfCircle CenterX=58.5 CenterY=15.1 CenterZ=0 NormalX=0 NormalY=0 NormalZ=1 AngleXU=0 Radius=2 StartAngle=4.71239 EndAngle=7.85398
    g14: LineSegment StartX=51.5 StartY=13.1 StartZ=0 EndX=58.5 EndY=13.1 EndZ=0
    g15: LineSegment StartX=58.5 StartY=17.1 StartZ=0 EndX=51.5 EndY=17.1 EndZ=0
  constraints (40):
    c: Tangent(g0,g2) = -1.5708
    c: Tangent(g2,g1) = -1.5708
    c: Tangent(g1,g3) = -1.5708
    c: Tangent(g3,g0) = -1.5708
    c: Equal(g0,g1)
    c: Horizontal(g2)
    c: DistanceX(g0) = 11.55
    c: DistanceX(g0,g1) = 2
    c: DistanceY(g0) = 15.58
    c: DistanceY(g0,g0) = 2.5
    c: Tangent(g4,g6) = -1.5708
    c: Tangent(g6,g5) = -1.5708
    c: Tangent(g5,g7) = -1.5708
    c: Tangent(g7,g4) = -1.5708
    c: Equal(g4,g5)
    c: Horizontal(g6)
    c: DistanceY(g4,g1) = 0
    c: DistanceX(g4,g5) = 2
    c: DistanceX(g1,g4) = 30.47
    c: DistanceY(g4,g4) = 2.5
    c: Tangent(g8,g10) = -1.5708
    c: Tangent(g10,g9) = -1.5708
    c: Tangent(g9,g11) = -1.5708
    c: Tangent(g11,g8) = -1.5708
    c: Equal(g8,g9)
    c: Horizontal(g10)
    c: DistanceX(g8) = 16.9
    c: DistanceY(g8,g8) = 2.15
    c: DistanceX(g8,g9) = 6.6
    c: DistanceY(g8) = 16.35
    c: Tangent(g12,g14) = -1.5708
    c: Tangent(g14,g13) = -1.5708
    c: Tangent(g13,g15) = -1.5708
    c: Tangent(g15,g12) = -1.5708
    c: Equal(g12,g13)
    c: Horizontal(g14)
    c: DistanceX(g12) = 51.5
    c: DistanceX(g12,g13) = 7
    c: DistanceY(g12) = 15.1
    c: DistanceY(g12,g12) = 4
FEATURE [Part::Extrusion] Extrude004  label="lightBottomCut"
  Base = -> Sketch004
  Dir = (0,-1,-3e-16)
  DirMode = 2
  FaceMakerClass = Part::FaceMakerBullseye
  LengthFwd = 2
  LengthRev = 0
  Placement = pos=(0,2,0) rot=(0,0,1;0rad)
  Solid = true
  Symmetric = false
FEATURE [Sketcher::SketchObject] Sketch005
  FullyConstrained = true
  Placement = pos=(0,0,0) rot=(1,0,0;1.5708rad)
  sketch-geometry (4):
    g0: ArcOfCircle CenterX=16.9 CenterY=16.35 CenterZ=0 NormalX=0 NormalY=0 NormalZ=1 AngleXU=0 Radius=1 StartAngle=1.5708 EndAngle=4.71239
    g1: ArcOfCircle CenterX=23.5 CenterY=16.35 CenterZ=0 NormalX=0 NormalY=0 NormalZ=1 AngleXU=0 Radius=1 StartAngle=4.71239 EndAngle=7.85398
    g2: LineSegment StartX=16.9 StartY=15.35 StartZ=0 EndX=23.5 EndY=15.35 EndZ=0
    g3: LineSegment StartX=23.5 StartY=17.35 StartZ=0 EndX=16.9 EndY=17.35 EndZ=0
  constraints (10):
    c: Tangent(g0,g2) = -1.5708
    c: Tangent(g2,g1) = -1.5708
    c: Tangent(g1,g3) = -1.5708
    c: Tangent(g3,g0) = -1.5708
    c: Equal(g0,g1)
    c: Horizontal(g2)
    c: DistanceX(g0) = 16.9
    c: DistanceY(g0,g0) = 2
    c: DistanceX(g0,g1) = 6.6
    c: DistanceY(g0) = 16.35
FEATURE [Sketcher::SketchObject] Sketch006
  FullyConstrained = true
  Placement = pos=(0,0,0) rot=(1,0,0;1.5708rad)
  sketch-geometry (4):
    g0: ArcOfCircle CenterX=16.9 CenterY=14.75 CenterZ=0 NormalX=0 NormalY=0 NormalZ=1 AngleXU=0 Radius=1 StartAngle=1.5708 EndAngle=4.71239
    g1: ArcOfCircle CenterX=23.5 CenterY=14.75 CenterZ=0 NormalX=0 NormalY=0 NormalZ=1 AngleXU=0 Radius=1 StartAngle=4.71239 EndAngle=7.85398
    g2: LineSegment StartX=16.9 StartY=13.75 StartZ=0 EndX=23.5 EndY=13.75 EndZ=0
    g3: LineSegment StartX=23.5 StartY=15.75 StartZ=0 EndX=16.9 EndY=15.75 EndZ=0
  constraints (10):
    c: Tangent(g0,g2) = -1.5708
    c: Tangent(g2,g1) = -1.5708
    c: Tangent(g1,g3) = -1.5708
    c: Tangent(g3,g0) = -1.5708
    c: Equal(g0,g1)
    c: Horizontal(g2)
    c: DistanceX(g0) = 16.9
    c: DistanceY(g0,g0) = 2
    c: DistanceX(g0,g1) = 6.6
    c: DistanceY(g0) = 14.75
FEATURE [Part::Extrusion] Extrude005
  Base = -> Sketch005
  Dir = (0,-1,2e-16)
  DirMode = 2
  FaceMakerClass = Part::FaceMakerBullseye
  LengthFwd = 2.25
  LengthRev = 0
  Placement = pos=(0,2,0) rot=(0,0,1;0rad)
  Solid = true
  Symmetric = false
FEATURE [Part::Extrusion] Extrude006
  Base = -> Sketch006
  Dir = (0,-1,2e-16)
  DirMode = 2
  FaceMakerClass = Part::FaceMakerBullseye
  LengthFwd = 2
  LengthRev = 0
  Placement = pos=(0,4,0) rot=(0,0,1;0rad)
  Solid = true
  Symmetric = false
FEATURE [Part::MultiFuse] Fusion008  label="lightInlet"
  Placement = pos=(0,0.25,0) rot=(0,0,1;0rad)
  Shapes = -> [Extrude005,Extrude006]
FEATURE [Sketcher::SketchObject] Sketch007
  FullyConstrained = true
  sketch-geometry (48):
    g0: LineSegment StartX=4 StartY=77 StartZ=0 EndX=6 EndY=77 EndZ=0
    g1: LineSegment StartX=6 StartY=77 StartZ=0 EndX=-3.99999 EndY=59.6795 EndZ=0
    g2: LineSegment StartX=-3.99999 StartY=59.6795 StartZ=0 EndX=-5.99999 EndY=59.6795 EndZ=0
    g3: LineSegment StartX=-5.99999 StartY=59.6795 StartZ=0 EndX=4 EndY=77 EndZ=0
    g4: LineSegment StartX=-5.99999 StartY=52.6795 StartZ=0 EndX=-3.99999 EndY=52.6795 EndZ=0
    g5: LineSegment StartX=-5.99999 StartY=52.6795 StartZ=0 EndX=4 EndY=70 EndZ=0
    g6: LineSegment StartX=4 StartY=70 StartZ=0 EndX=6 EndY=70 EndZ=0
    g7: LineSegment StartX=6 StartY=70 StartZ=0 EndX=-3.99999 EndY=52.6795 EndZ=0
    g8: LineSegment StartX=-3.99999 StartY=45.6795 StartZ=0 EndX=-5.99999 EndY=45.6795 EndZ=0
    g9: LineSegment StartX=-5.99999 StartY=45.6795 StartZ=0 EndX=4 EndY=63 EndZ=0
    g10: LineSegment StartX=4 StartY=63 StartZ=0 EndX=6 EndY=63 EndZ=0
    g11: LineSegment StartX=6 StartY=63 StartZ=0 EndX=-3.99999 EndY=45.6795 EndZ=0
    g12: LineSegment StartX=4 StartY=56 StartZ=0 EndX=6 EndY=56 EndZ=0
    g13: LineSegment StartX=6 StartY=56 StartZ=0 EndX=-3.99999 EndY=38.6795 EndZ=0
    g14: LineSegment StartX=-3.99999 StartY=38.6795 StartZ=0 EndX=-5.99999 EndY=38.6795 EndZ=0
    g15: LineSegment StartX=-5.99999 StartY=38.6795 StartZ=0 EndX=4 EndY=56 EndZ=0
    g16: LineSegment StartX=4 StartY=49 StartZ=0 EndX=6 EndY=49 EndZ=0
    g17: LineSegment StartX=6 StartY=49 StartZ=0 EndX=-3.99999 EndY=31.6795 EndZ=0
    g18: LineSegment StartX=-3.99999 StartY=31.6795 StartZ=0 EndX=-5.99999 EndY=31.6795 EndZ=0
    g19: LineSegment StartX=-5.99999 StartY=31.6795 StartZ=0 EndX=4 EndY=49 EndZ=0
    g20: LineSegment StartX=4 StartY=42 StartZ=0 EndX=6 EndY=42 EndZ=0
    g21: LineSegment StartX=6 StartY=42 StartZ=0 EndX=-3.99999 EndY=24.6795 EndZ=0
    g22: LineSegment StartX=-3.99999 StartY=24.6795 StartZ=0 EndX=-5.99999 EndY=24.6795 EndZ=0
    g23: LineSegment StartX=-5.99999 StartY=24.6795 StartZ=0 EndX=4 EndY=42 EndZ=0
    g24: LineSegment StartX=66 StartY=77 StartZ=0 EndX=64 EndY=77 EndZ=0
    g25: LineSegment StartX=64 StartY=77 StartZ=0 EndX=74 EndY=59.6795 EndZ=0
    g26: LineSegment StartX=74 StartY=59.6795 StartZ=0 EndX=76 EndY=59.6795 EndZ=0
    g27: LineSegment StartX=76 StartY=59.6795 StartZ=0 EndX=66 EndY=77 EndZ=0
    g28: LineSegment StartX=64 StartY=70 StartZ=0 EndX=66 EndY=70 EndZ=0
    g29: LineSegment StartX=66 StartY=70 StartZ=0 EndX=76 EndY=52.6795 EndZ=0
    g30: LineSegment StartX=76 StartY=52.6795 StartZ=0 EndX=74 EndY=52.6795 EndZ=0
    g31: LineSegment StartX=74 StartY=52.6795 StartZ=0 EndX=64 EndY=70 EndZ=0
    g32: LineSegment StartX=64 StartY=63 StartZ=0 EndX=66 EndY=63 EndZ=0
    g33: LineSegment StartX=66 StartY=63 StartZ=0 EndX=76 EndY=45.6795 EndZ=0
    g34: LineSegment StartX=76 StartY=45.6795 StartZ=0 EndX=74 EndY=45.6795 EndZ=0
    g35: LineSegment StartX=74 StartY=45.6795 StartZ=0 EndX=64 EndY=63 EndZ=0
    g36: LineSegment StartX=64 StartY=56 StartZ=0 EndX=66 EndY=56 EndZ=0
    g37: LineSegment StartX=66 StartY=56 StartZ=0 EndX=76 EndY=38.6795 EndZ=0
    g38: LineSegment StartX=76 StartY=38.6795 StartZ=0 EndX=74 EndY=38.6795 EndZ=0
    g39: LineSegment StartX=74 StartY=38.6795 StartZ=0 EndX=64 EndY=56 EndZ=0
    g40: LineSegment StartX=64 StartY=49 StartZ=0 EndX=66 EndY=49 EndZ=0
    g41: LineSegment StartX=66 StartY=49 StartZ=0 EndX=76 EndY=31.6795 EndZ=0
    g42: LineSegment StartX=76 StartY=31.6795 StartZ=0 EndX=74 EndY=31.6795 EndZ=0
    g43: LineSegment StartX=74 StartY=31.6795 StartZ=0 EndX=64 EndY=49 EndZ=0
    g44: LineSegment StartX=64 StartY=42 StartZ=0 EndX=66 EndY=42 EndZ=0
    g45: LineSegment StartX=66 StartY=42 StartZ=0 EndX=76 EndY=24.6795 EndZ=0
    g46: LineSegment StartX=76 StartY=24.6795 StartZ=0 EndX=74 EndY=24.6795 EndZ=0
    g47: LineSegment StartX=74 StartY=24.6795 StartZ=0 EndX=64 EndY=42 EndZ=0
  constraints (144):
    c: Coincident(g3,g0)
    c: DistanceX(g2,g2) = 2
    c: DistanceX(g0,g0) = 2
    c: Angle(g1) = -2.0944
    c: Distance(g3) = 20
    c: Coincident(g2,g3)
    c: DistanceX(g0) = 4
    c: DistanceY(g0) = 77
    c: Coincident(g4,g5)
    c: Coincident(g6,g7)
    c: Coincident(g7,g4)
    c: Horizontal(g6)
    c: DistanceX(g5,g0) = 0
    c: DistanceY(g5,g0) = 7
    c: DistanceX(g2,g4) = 0
    c: DistanceX(g1,g4) = 0
    c: DistanceY(g4,g2) = 7
    c: Horizontal(g4)
    c: Angle(g5) = 1.0472
    c: Horizontal(g8)
    c: Coincident(g9,g8)
    c: Horizontal(g10)
    c: Coincident(g11,g8)
    c: Coincident(g9,g10)
    c: Coincident(g10,g11)
    c: DistanceX(g5,g9) = 0
    c: DistanceX(g10,g6) = 0
    c: DistanceY(g9,g5) = 7
    c: DistanceY(g8,g4) = 7
    c: DistanceX(g8,g4) = 0
    c: DistanceX(g4,g8) = 0
    c: Horizontal(g12)
    c: Coincident(g13,g12)
    c: Horizontal(g14)
    c: Coincident(g15,g12)
    c: Coincident(g1,g2)
    c: Horizontal(g2)
    c: DistanceX(g12,g12) = 2
    c: DistanceX(g9,g12) = 0
    c: DistanceY(g12,g9) = 7
    c: DistanceY(g14,g8) = 7
    c: Coincident(g14,g13)
    c: Coincident(g14,g15)
    c: DistanceX(g14,g8) = 0
    c: DistanceX(g8,g13) = 0
    c: Horizontal(g16)
    c: Coincident(g17,g16)
    c: Horizontal(g18)
    c: Coincident(g19,g16)
    c: DistanceX(g16,g16) = 2
    c: DistanceY(g16,g12) = 7
    c: DistanceX(g12,g16) = 0
    c: DistanceX(g18,g14) = 0
    c: Coincident(g18,g19)
    c: Coincident(g17,g18)
    c: DistanceY(g18,g14) = 7
    c: DistanceX(g18,g18) = 2
    c: Horizontal(g20)
    c: Coincident(g20,g21)
    c: Coincident(g21,g22)
    c: Coincident(g22,g23)
    c: Coincident(g23,g20)
    c: DistanceX(g16,g20) = 0
    c: DistanceY(g20,g16) = 7
    c: DistanceY(g22,g18) = 7
    c: DistanceX(g22,g18) = 0
    c: Horizontal(g22)
    c: DistanceX(g22,g22) = 2
    c: DistanceX(g20,g20) = 2
    c: Horizontal(g24)
    c: Coincident(g25,g24)
    c: Coincident(g26,g25)
    c: Horizontal(g26)
    c: Coincident(g27,g24)
    c: DistanceX(g24,g24) = 2
    c: DistanceX(g0,g24) = 62
    c: DistanceY(g24,g0) = 0
    c: Distance(g25) = 20
    c: Coincident(g26,g27)
    c: Angle(g27) = 2.0944
    c: DistanceX(g26,g26) = 2
    c: Horizontal(g28)
    c: Coincident(g29,g28)
    c: Coincident(g30,g29)
    c: Coincident(g31,g28)
    c: Coincident(g33,g32)
    c: Coincident(g34,g33)
    c: Coincident(g35,g32)
    c: Coincident(g37,g36)
    c: Coincident(g38,g37)
    c: Coincident(g39,g36)
    c: DistanceY(g28,g6) = 0
    c: DistanceY(g32,g9) = 0
    c: DistanceY(g36,g12) = 0
    c: DistanceX(g24,g28) = 0
    c: DistanceX(g32,g28) = 0
    c: DistanceX(g36,g32) = 0
    c: Horizontal(g36)
    c: Horizontal(g32)
    c: DistanceX(g32,g32) = 2
    c: DistanceX(g36,g36) = 2
    c: Horizontal(g30)
    c: Horizontal(g34)
    c: Horizontal(g38)
    c: Coincident(g34,g35)
    c: Coincident(g30,g31)
    c: DistanceX(g25,g30) = 0
    c: DistanceX(g30,g34) = 0
    c: DistanceX(g34,g34) = 2
    c: DistanceX(g30,g30) = 2
    c: Coincident(g38,g39)
    c: DistanceX(g38,g38) = 2
    c: DistanceX(g34,g38) = 0
    c: Horizontal(g40)
    c: Coincident(g41,g40)
    c: Horizontal(g42)
    c: Coincident(g43,g40)
    c: DistanceY(g40,g16) = 0
    c: Horizontal(g44)
    c: Coincident(g45,g44)
    c: Coincident(g46,g45)
    c: Horizontal(g46)
    c: Coincident(g47,g44)
    c: DistanceY(g20,g44) = 0
    c: DistanceX(g44,g40) = 0
    c: DistanceX(g40,g36) = 0
    c: DistanceX(g44,g44) = 2
    c: DistanceX(g40,g40) = 2
    c: DistanceX(g46,g46) = 2
    c: DistanceX(g42,g42) = 2
    c: Coincident(g42,g43)
    c: Coincident(g41,g42)
    c: Coincident(g46,g47)
    c: DistanceX(g42,g38) = 0
    c: DistanceX(g46,g42) = 0
    c: DistanceY(g46,g42) = 7
    c: DistanceY(g42,g38) = 7
    c: DistanceY(g38,g34) = 7
    c: DistanceY(g34,g30) = 7
    c: DistanceY(g30,g25) = 7
    c: DistanceX(g28,g28) = 2
    c: Coincident(g0,g1)
    c: DistanceX(g6,g6) = 2
    c: Coincident(g5,g6)
FEATURE [Part::Extrusion] Extrude007  label="ventsBottomCut"
  Base = -> Sketch007
  Dir = (0,0,1)
  DirMode = 2
  FaceMakerClass = Part::FaceMakerBullseye
  LengthFwd = 20
  LengthRev = 0
  Placement = pos=(0,0,5) rot=(0,0,1;0rad)
  Solid = true
  Symmetric = false
FEATURE [Part::Cylinder] Cylinder016
  Angle = 360
  AttacherType = Attacher::AttachEngine3D
  FirstAngle = 0
  Height = 14
  Placement = pos=(7.25,73.75,2) rot=(0,0,1;0rad)
  Radius = 2.1
  SecondAngle = 0
FEATURE [Part::Cylinder] Cylinder017
  Angle = 360
  AttacherType = Attacher::AttachEngine3D
  FirstAngle = 0
  Height = 14
  Placement = pos=(62.75,38,2) rot=(0,0,1;0rad)
  Radius = 2.1
  SecondAngle = 0
FEATURE [Part::Cylinder] Cylinder018
  Angle = 360
  AttacherType = Attacher::AttachEngine3D
  FirstAngle = 0
  Height = 14
  Placement = pos=(7.25,38,2) rot=(0,0,1;0rad)
  Radius = 2.1
  SecondAngle = 0
FEATURE [Part::Cylinder] Cylinder019
  Angle = 360
  AttacherType = Attacher::AttachEngine3D
  FirstAngle = 0
  Height = 14
  Placement = pos=(62.75,73.75,2) rot=(0,0,1;0rad)
  Radius = 2.1
  SecondAngle = 0
FEATURE [Part::MultiFuse] Fusion009  label="basesM4TopCut"
  Placement = pos=(0,0,12.25) rot=(0,0,1;0rad)
  Shapes = -> [Cylinder019,Cylinder016,Cylinder017,Cylinder018]
FEATURE [Sketcher::SketchObject] Sketch008
  FullyConstrained = true
  MapMode = 2
  Placement = pos=(0,0,12.25) rot=(0,0,1;0rad)
  Support = -> [Fusion009]
  sketch-geometry (10):
    g0: LineSegment StartX=2.5 StartY=78.5 StartZ=0 EndX=2.5 EndY=2.5 EndZ=0
    g1: LineSegment StartX=2.5 StartY=2.5 StartZ=0 EndX=35 EndY=2.5 EndZ=0
    g2: LineSegment StartX=67.5 StartY=21.25 StartZ=0 EndX=67.5 EndY=78.5 EndZ=0
    g3: LineSegment StartX=2.5 StartY=78.5 StartZ=0 EndX=67.5 EndY=78.5 EndZ=0
    g4: LineSegment StartX=35 StartY=2.5 StartZ=0 EndX=35 EndY=3.5 EndZ=0
    g5: LineSegment StartX=35 StartY=3.5 StartZ=0 EndX=3.5 EndY=3.5 EndZ=0
    g6: LineSegment StartX=3.5 StartY=3.5 StartZ=0 EndX=3.5 EndY=77.5 EndZ=0
    g7: LineSegment StartX=3.5 StartY=77.5 StartZ=0 EndX=66.5 EndY=77.5 EndZ=0
    g8: LineSegment StartX=66.5 StartY=77.5 StartZ=0 EndX=66.5 EndY=21.25 EndZ=0
    g9: LineSegment StartX=66.5 StartY=21.25 StartZ=0 EndX=67.5 EndY=21.25 EndZ=0
  constraints (30):
    c: Vertical(g0)
    c: Horizontal(g1)
    c: Vertical(g2)
    c: Coincident(g3,g2)
    c: DistanceX(g-1,g0) = 2.5
    c: DistanceY(g0) = 2.5
    c: Coincident(g1,g0)
    c: Coincident(g0,g3)
    c: Coincident(g4,g1)
    c: Vertical(g4)
    c: Horizontal(g5)
    c: Coincident(g6,g5)
    c: Vertical(g6)
    c: Horizontal(g7)
    c: Coincident(g8,g7)
    c: Vertical(g8)
    c: Coincident(g9,g8)
    c: Coincident(g9,g2)
    c: DistanceX(g5) = 3.5
    c: DistanceY(g-1,g5) = 3.5
    c: DistanceX(g0,g1) = 32.5
    c: Coincident(g5,g4)
    c: Coincident(g6,g7)
    c: DistanceY(g0,g0) = 76
    c: DistanceY(g6,g0) = 1
    c: DistanceX(g7,g2) = 1
    c: DistanceX(g0,g2) = 65
    c: Horizontal(g9)
    c: DistanceY(g8,g7) = 56.25
    c: Horizontal(g3)
FEATURE [Part::Extrusion] Extrude008  label="topAlineIn"
  Base = -> Sketch008
  Dir = (0,0,1)
  DirMode = 2
  FaceMakerClass = Part::FaceMakerBullseye
  LengthFwd = 1.5
  LengthRev = 0
  Placement = pos=(0,0,15) rot=(0,0,1;0rad)
  Solid = true
  Symmetric = false
FEATURE [Part::MultiFuse] Fusion010  label="topIn"
  Shapes = -> [Extrude008,Fusion002,Fillet005]
FEATURE [Part::MultiFuse] Fusion011  label="topCut"
  Shapes = -> [Fusion009,Part__Feature060,Box005,Extrude003]
FEATURE [Part::Cut] Cut001  label="top002"
  Base = -> Fusion010
  Tool = -> Fusion011
FEATURE [Part::Fillet] Fillet006  label="top003"
  Base = -> Cut001
  Edges = 22 edges r=0.25: [Edge1,Edge5,Edge7,Edge8,Edge941,Edge944,Edge2741,Edge2754,Edge2756,Edge2758,Edge2760,Edge2762,Edge2782,Edge2784,Edge2786,Edge2787,Edge2802,Edge2804,Edge2814,Edge2842,Edge2857,Edge2858]
FEATURE [Part::Cut] Cut002  label="bottom004"
  Base = -> Cut
  Tool = -> Extrude007
FEATURE [Part::MultiFuse] Fusion014  label="bottomCuts"
  Shapes = -> [Extrude004,Fusion007,Fusion001]
FEATURE [Part::Box] Box006  label="ipsCut"
  AttacherType = Attacher::AttachEngine3D
  Height = 14
  Length = 48.15
  Placement = pos=(10.9,33,2) rot=(0,0,1;0rad)
  Width = 44
FEATURE [Part::Cut] Cut003  label="bottomBasesIn"
  Base = -> Fusion
  Tool = -> Box006
FEATURE [Part::MultiFuse] Fusion015  label="bottom005"
  Shapes = -> [Cut003,Cut002,Fillet004,Fillet003]
FEATURE [Part::Cut] Cut004  label="bottom006"
  Base = -> Fusion015
  Tool = -> Fusion014
FEATURE [Part::Fillet] Fillet007
  Base = -> Cut004
  Edges = 12 edges r=1: [Edge352,Edge353,Edge354,Edge355,Edge360,Edge361,Edge362,Edge363,Edge364,Edge365,Edge366,Edge367]
FEATURE [Part::Fillet] Fillet008
  Base = -> Fillet007
  Edges = 48 edges r=0.5: [Edge85,Edge86,Edge87,Edge88,Edge89,Edge90,Edge91,Edge92,Edge93,Edge94,Edge95,Edge96,Edge97,Edge98,Edge99,Edge100,Edge101,Edge102,Edge103,Edge104,Edge105,Edge106,Edge107,Edge108,Edge116,Edge117,Edge118,Edge119,Edge120,Edge121,Edge122,Edge123,Edge124,Edge125,Edge126,Edge127,Edge128,Edge129,Edge130,+9 more]
FEATURE [Part::Fillet] Fillet009  label="bottom007"
  Base = -> Fillet008
  Edges = 68 edges r=0.5: [Edge32,Edge34,Edge35,Edge37,Edge66,Edge68,Edge69,Edge71,Edge79,Edge82,Edge85,Edge90,Edge92,Edge95,Edge102,Edge104,Edge107,Edge114,Edge116,Edge119,Edge123,Edge125,Edge287,Edge288,Edge292,Edge294,Edge295,Edge296,Edge299,Edge300,Edge303,Edge304,Edge342,Edge344,Edge345,Edge352,Edge353,Edge357,Edge360,+29 more]
FEATURE [Sketcher::SketchObject] Sketch009
  FullyConstrained = true
  MapMode = 4
  Placement = pos=(0,0,0) rot=(0.57735,0.57735,0.57735;2.0944rad)
  Support = -> [Fillet009]
  sketch-geometry (1):
    g0: Circle CenterX=79 CenterY=2 CenterZ=0 NormalX=0 NormalY=0 NormalZ=1 AngleXU=0 Radius=2
  constraints (3):
    c: DistanceX(g0) = 79
    c: DistanceY(g0) = 2
    c: Radius(g0) = 2
FEATURE [Part::Extrusion] Extrude009  label="bottomInTagHold"
  Base = -> Sketch009
  Dir = (1,0,0)
  DirMode = 2
  FaceMakerClass = Part::FaceMakerBullseye
  LengthFwd = 66
  LengthRev = 0
  Placement = pos=(2,0,0) rot=(0,0,1;0rad)
  Solid = true
  Symmetric = false
FEATURE [Sketcher::SketchObject] Sketch010
  FullyConstrained = true
  Placement = pos=(0,0,0) rot=(0.57735,0.57735,0.57735;2.0944rad)
  sketch-geometry (2):
    g0: Circle CenterX=79 CenterY=2 CenterZ=0 NormalX=0 NormalY=0 NormalZ=1 AngleXU=0 Radius=3
    g1: Circle CenterX=79 CenterY=2 CenterZ=0 NormalX=0 NormalY=0 NormalZ=1 AngleXU=0 Radius=2
  constraints (5):
    c: Radius(g0) = 3
    c: Radius(g1) = 2
    c: Coincident(g0,g1)
    c: DistanceX(g0) = 79
    c: DistanceY(g0) = 2
FEATURE [Part::Extrusion] Extrude010  label="tagBottomCut"
  Base = -> Sketch010
  Dir = (1,-1e-16,0)
  DirMode = 2
  FaceMakerClass = Part::FaceMakerBullseye
  LengthFwd = 10
  LengthRev = 0
  Placement = pos=(15,0,0) rot=(0,0,1;0rad)
  Solid = true
  Symmetric = false
FEATURE [Sketcher::SketchObject] Sketch011
  FullyConstrained = true
  Placement = pos=(0,0,0) rot=(0.57735,0.57735,0.57735;2.0944rad)
  sketch-geometry (2):
    g0: Circle CenterX=79 CenterY=2 CenterZ=0 NormalX=0 NormalY=0 NormalZ=1 AngleXU=0 Radius=3
    g1: Circle CenterX=79 CenterY=2 CenterZ=0 NormalX=0 NormalY=0 NormalZ=1 AngleXU=0 Radius=2
  constraints (5):
    c: Radius(g0) = 3
    c: Radius(g1) = 2
    c: Coincident(g0,g1)
    c: DistanceX(g0) = 79
    c: DistanceY(g0) = 2
FEATURE [Part::Extrusion] Extrude011  label="tagBottomCut001"
  Base = -> Sketch011
  Dir = (1,0,0)
  DirMode = 2
  FaceMakerClass = Part::FaceMakerBullseye
  LengthFwd = 10
  LengthRev = 0
  Placement = pos=(30,0,0) rot=(0,0,1;0rad)
  Solid = true
  Symmetric = false
FEATURE [Sketcher::SketchObject] Sketch012
  FullyConstrained = true
  Placement = pos=(0,0,0) rot=(0.57735,0.57735,0.57735;2.0944rad)
  sketch-geometry (2):
    g0: Circle CenterX=79 CenterY=2 CenterZ=0 NormalX=0 NormalY=0 NormalZ=1 AngleXU=0 Radius=3
    g1: Circle CenterX=79 CenterY=2 CenterZ=0 NormalX=0 NormalY=0 NormalZ=1 AngleXU=0 Radius=2
  constraints (5):
    c: Radius(g0) = 3
    c: Radius(g1) = 2
    c: Coincident(g0,g1)
    c: DistanceX(g0) = 79
    c: DistanceY(g0) = 2
FEATURE [Part::Extrusion] Extrude012  label="tagBottomCut002"
  Base = -> Sketch012
  Dir = (1,0,0)
  DirMode = 2
  FaceMakerClass = Part::FaceMakerBullseye
  LengthFwd = 10
  LengthRev = 0
  Placement = pos=(45,0,0) rot=(0,0,1;0rad)
  Solid = true
  Symmetric = false
FEATURE [Part::MultiFuse] Fusion016  label="bottomCuts001"
  Shapes = -> [Extrude010,Extrude011,Extrude012]
FEATURE [Part::MultiFuse] Fusion017  label="bottomIn"
  Shapes = -> [Fillet009,Extrude009]
FEATURE [Part::Cut] Cut005  label="bottom008"
  Base = -> Fusion017
  Tool = -> Fusion016
FEATURE [Part::Fillet] Fillet010
  Base = -> Cut005
  Edges = 6 edges r=1: [Edge10,Edge14,Edge18,Edge28,Edge32,Edge36]
FEATURE [Part::Fillet] Fillet011
  Base = -> Fillet010
  Edges = 12 edges r=1: [Edge1,Edge3,Edge10,Edge14,Edge16,Edge20,Edge98,Edge102,Edge106,Edge107,Edge111,Edge112]
FEATURE [Part::Fillet] Fillet012  label="bottom009"
  Base = -> Fillet011
  Edges = 4 edges r=0.25: [Edge156,Edge157,Edge158,Edge159]
